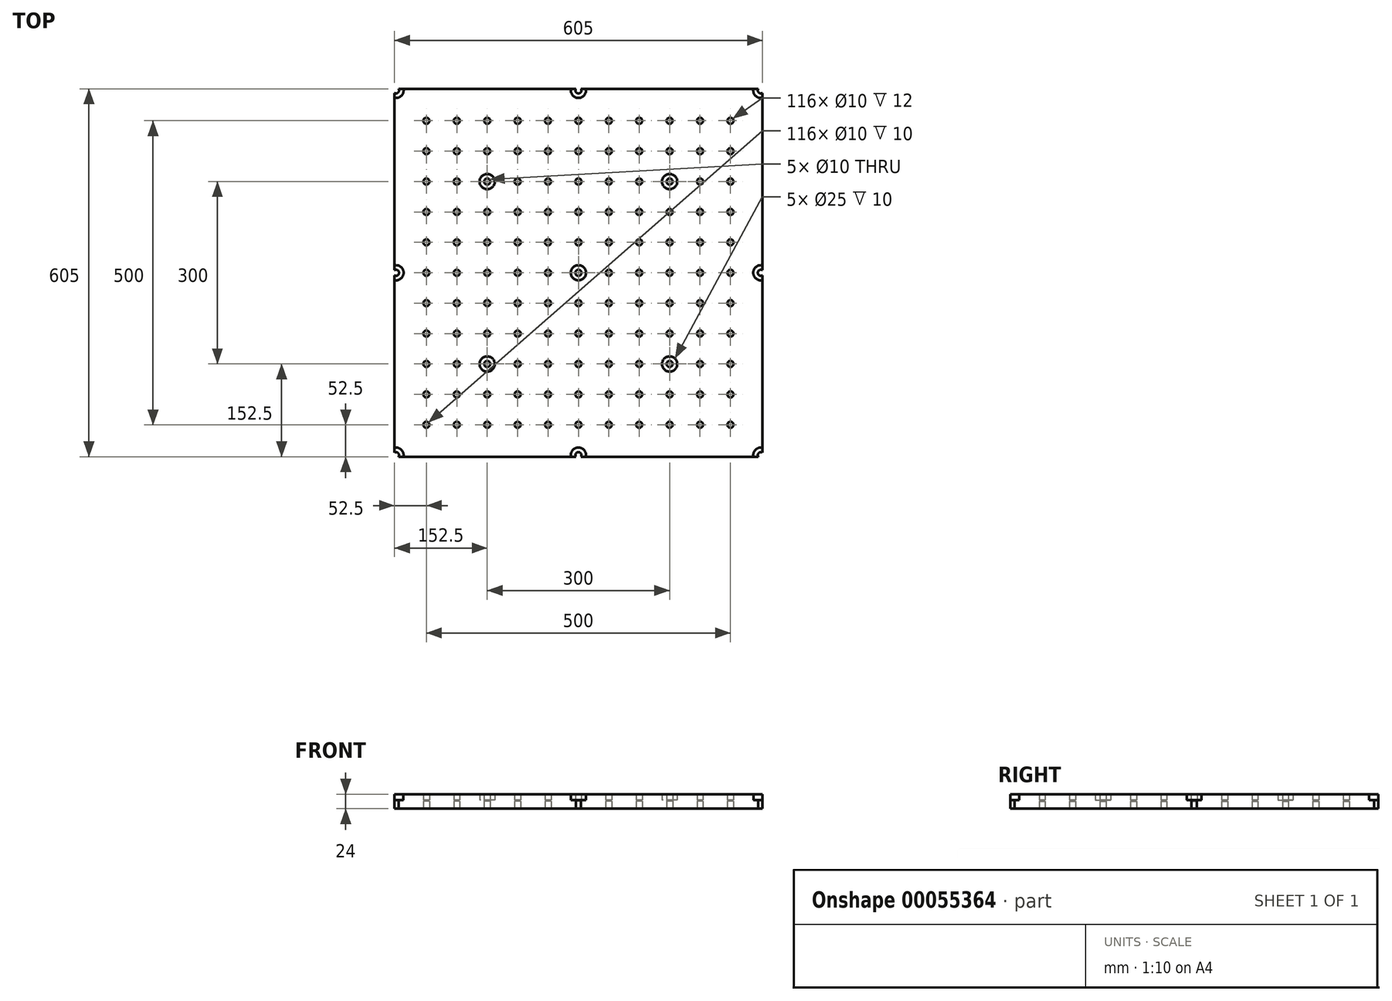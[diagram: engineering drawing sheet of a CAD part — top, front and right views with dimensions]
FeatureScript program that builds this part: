
annotation { "Feature Type Name" : "Feature", "Feature Type Description" : "" }
export const myFeature = defineFeature(function(context is Context, id is Id, definition is map)
    precondition{}
    {
        {
            var Q0;
            Q0=qCreatedBy(makeId("Top.planeOp"),FACE);
            var sketch = newSketch(context, id + "F0", { "sketchPlane" : qUnion([Q0])});
            skLineSegment(sketch, "E0.rect.bottom", {"start": v(295.67, 302.5) * mm, "end": v(4.33, 302.5) * mm});
            skLineSegment(sketch, "E0.rect.top", {"start": v(295.67, -302.5) * mm, "end": v(4.33, -302.5) * mm});
            skLineSegment(sketch, "E0.rect.left", {"start": v(302.5, 295.67) * mm, "end": v(302.5, 4.33) * mm});
            skLineSegment(sketch, "E0.rect.right", {"start": v(-302.5, 295.67) * mm, "end": v(-302.5, 4.33) * mm});
            skPoint(sketch, "E0.rect.middle", {"position": v(0, 0) * mm});
            skArc(sketch, "E1", {"start": v(-295.67, -302.5) * mm, "mid": v(-296.46, -296.46) * mm, "end": v(-302.5, -295.67) * mm});
            skCircle(sketch, "E2.0.1.0", {"center": v(-300, -250) * mm, "radius": 5 * mm, "construction": true});
            skCircle(sketch, "E2.0.2.0", {"center": v(-300, -200) * mm, "radius": 5 * mm, "construction": true});
            skCircle(sketch, "E2.0.3.0", {"center": v(-300, -150) * mm, "radius": 5 * mm, "construction": true});
            skCircle(sketch, "E2.0.4.0", {"center": v(-300, -100) * mm, "radius": 5 * mm, "construction": true});
            skCircle(sketch, "E2.0.5.0", {"center": v(-300, -50) * mm, "radius": 5 * mm, "construction": true});
            skArc(sketch, "E2.0.6.0", {"start": v(-302.5, -4.33) * mm, "mid": v(-295, 0) * mm, "end": v(-302.5, 4.33) * mm});
            skCircle(sketch, "E2.0.7.0", {"center": v(-300, 50) * mm, "radius": 5 * mm, "construction": true});
            skCircle(sketch, "E2.0.8.0", {"center": v(-300, 100) * mm, "radius": 5 * mm, "construction": true});
            skCircle(sketch, "E2.0.9.0", {"center": v(-300, 150) * mm, "radius": 5 * mm, "construction": true});
            skCircle(sketch, "E2.0.10.0", {"center": v(-300, 200) * mm, "radius": 5 * mm, "construction": true});
            skCircle(sketch, "E2.0.11.0", {"center": v(-300, 250) * mm, "radius": 5 * mm, "construction": true});
            skArc(sketch, "E2.0.12.0", {"start": v(-302.5, 295.67) * mm, "mid": v(-296.46, 296.46) * mm, "end": v(-295.67, 302.5) * mm});
            skCircle(sketch, "E2.1.0.0", {"center": v(-250, -300) * mm, "radius": 5 * mm, "construction": true});
            skCircle(sketch, "E2.1.1.0", {"center": v(-250, -250) * mm, "radius": 5 * mm});
            skCircle(sketch, "E2.1.2.0", {"center": v(-250, -200) * mm, "radius": 5 * mm});
            skCircle(sketch, "E2.1.3.0", {"center": v(-250, -150) * mm, "radius": 5 * mm});
            skCircle(sketch, "E2.1.4.0", {"center": v(-250, -100) * mm, "radius": 5 * mm});
            skCircle(sketch, "E2.1.5.0", {"center": v(-250, -50) * mm, "radius": 5 * mm});
            skCircle(sketch, "E2.1.6.0", {"center": v(-250, 0) * mm, "radius": 5 * mm});
            skCircle(sketch, "E2.1.7.0", {"center": v(-250, 50) * mm, "radius": 5 * mm});
            skCircle(sketch, "E2.1.8.0", {"center": v(-250, 100) * mm, "radius": 5 * mm});
            skCircle(sketch, "E2.1.9.0", {"center": v(-250, 150) * mm, "radius": 5 * mm});
            skCircle(sketch, "E2.1.10.0", {"center": v(-250, 200) * mm, "radius": 5 * mm});
            skCircle(sketch, "E2.1.11.0", {"center": v(-250, 250) * mm, "radius": 5 * mm});
            skCircle(sketch, "E2.1.12.0", {"center": v(-250, 300) * mm, "radius": 5 * mm, "construction": true});
            skCircle(sketch, "E2.2.0.0", {"center": v(-200, -300) * mm, "radius": 5 * mm, "construction": true});
            skCircle(sketch, "E2.2.1.0", {"center": v(-200, -250) * mm, "radius": 5 * mm});
            skCircle(sketch, "E2.2.2.0", {"center": v(-200, -200) * mm, "radius": 5 * mm});
            skCircle(sketch, "E2.2.3.0", {"center": v(-200, -150) * mm, "radius": 5 * mm});
            skCircle(sketch, "E2.2.4.0", {"center": v(-200, -100) * mm, "radius": 5 * mm});
            skCircle(sketch, "E2.2.5.0", {"center": v(-200, -50) * mm, "radius": 5 * mm});
            skCircle(sketch, "E2.2.6.0", {"center": v(-200, 0) * mm, "radius": 5 * mm});
            skCircle(sketch, "E2.2.7.0", {"center": v(-200, 50) * mm, "radius": 5 * mm});
            skCircle(sketch, "E2.2.8.0", {"center": v(-200, 100) * mm, "radius": 5 * mm});
            skCircle(sketch, "E2.2.9.0", {"center": v(-200, 150) * mm, "radius": 5 * mm});
            skCircle(sketch, "E2.2.10.0", {"center": v(-200, 200) * mm, "radius": 5 * mm});
            skCircle(sketch, "E2.2.11.0", {"center": v(-200, 250) * mm, "radius": 5 * mm});
            skCircle(sketch, "E2.2.12.0", {"center": v(-200, 300) * mm, "radius": 5 * mm, "construction": true});
            skCircle(sketch, "E2.3.0.0", {"center": v(-150, -300) * mm, "radius": 5 * mm, "construction": true});
            skCircle(sketch, "E2.3.1.0", {"center": v(-150, -250) * mm, "radius": 5 * mm});
            skCircle(sketch, "E2.3.2.0", {"center": v(-150, -200) * mm, "radius": 5 * mm});
            skCircle(sketch, "E2.3.3.0", {"center": v(-150, -150) * mm, "radius": 5 * mm});
            skCircle(sketch, "E2.3.4.0", {"center": v(-150, -100) * mm, "radius": 5 * mm});
            skCircle(sketch, "E2.3.5.0", {"center": v(-150, -50) * mm, "radius": 5 * mm});
            skCircle(sketch, "E2.3.6.0", {"center": v(-150, 0) * mm, "radius": 5 * mm});
            skCircle(sketch, "E2.3.7.0", {"center": v(-150, 50) * mm, "radius": 5 * mm});
            skCircle(sketch, "E2.3.8.0", {"center": v(-150, 100) * mm, "radius": 5 * mm});
            skCircle(sketch, "E2.3.9.0", {"center": v(-150, 150) * mm, "radius": 5 * mm});
            skCircle(sketch, "E2.3.10.0", {"center": v(-150, 200) * mm, "radius": 5 * mm});
            skCircle(sketch, "E2.3.11.0", {"center": v(-150, 250) * mm, "radius": 5 * mm});
            skCircle(sketch, "E2.3.12.0", {"center": v(-150, 300) * mm, "radius": 5 * mm, "construction": true});
            skCircle(sketch, "E2.4.0.0", {"center": v(-100, -300) * mm, "radius": 5 * mm, "construction": true});
            skCircle(sketch, "E2.4.1.0", {"center": v(-100, -250) * mm, "radius": 5 * mm});
            skCircle(sketch, "E2.4.2.0", {"center": v(-100, -200) * mm, "radius": 5 * mm});
            skCircle(sketch, "E2.4.3.0", {"center": v(-100, -150) * mm, "radius": 5 * mm});
            skCircle(sketch, "E2.4.4.0", {"center": v(-100, -100) * mm, "radius": 5 * mm});
            skCircle(sketch, "E2.4.5.0", {"center": v(-100, -50) * mm, "radius": 5 * mm});
            skCircle(sketch, "E2.4.6.0", {"center": v(-100, 0) * mm, "radius": 5 * mm});
            skCircle(sketch, "E2.4.7.0", {"center": v(-100, 50) * mm, "radius": 5 * mm});
            skCircle(sketch, "E2.4.8.0", {"center": v(-100, 100) * mm, "radius": 5 * mm});
            skCircle(sketch, "E2.4.9.0", {"center": v(-100, 150) * mm, "radius": 5 * mm});
            skCircle(sketch, "E2.4.10.0", {"center": v(-100, 200) * mm, "radius": 5 * mm});
            skCircle(sketch, "E2.4.11.0", {"center": v(-100, 250) * mm, "radius": 5 * mm});
            skCircle(sketch, "E2.4.12.0", {"center": v(-100, 300) * mm, "radius": 5 * mm, "construction": true});
            skCircle(sketch, "E2.5.0.0", {"center": v(-50, -300) * mm, "radius": 5 * mm, "construction": true});
            skCircle(sketch, "E2.5.1.0", {"center": v(-50, -250) * mm, "radius": 5 * mm});
            skCircle(sketch, "E2.5.2.0", {"center": v(-50, -200) * mm, "radius": 5 * mm});
            skCircle(sketch, "E2.5.3.0", {"center": v(-50, -150) * mm, "radius": 5 * mm});
            skCircle(sketch, "E2.5.4.0", {"center": v(-50, -100) * mm, "radius": 5 * mm});
            skCircle(sketch, "E2.5.5.0", {"center": v(-50, -50) * mm, "radius": 5 * mm});
            skCircle(sketch, "E2.5.6.0", {"center": v(-50, 0) * mm, "radius": 5 * mm});
            skCircle(sketch, "E2.5.7.0", {"center": v(-50, 50) * mm, "radius": 5 * mm});
            skCircle(sketch, "E2.5.8.0", {"center": v(-50, 100) * mm, "radius": 5 * mm});
            skCircle(sketch, "E2.5.9.0", {"center": v(-50, 150) * mm, "radius": 5 * mm});
            skCircle(sketch, "E2.5.10.0", {"center": v(-50, 200) * mm, "radius": 5 * mm});
            skCircle(sketch, "E2.5.11.0", {"center": v(-50, 250) * mm, "radius": 5 * mm});
            skCircle(sketch, "E2.5.12.0", {"center": v(-50, 300) * mm, "radius": 5 * mm, "construction": true});
            skArc(sketch, "E2.6.0.0", {"start": v(4.33, -302.5) * mm, "mid": v(0, -295) * mm, "end": v(-4.33, -302.5) * mm});
            skCircle(sketch, "E2.6.1.0", {"center": v(0, -250) * mm, "radius": 5 * mm});
            skCircle(sketch, "E2.6.2.0", {"center": v(0, -200) * mm, "radius": 5 * mm});
            skCircle(sketch, "E2.6.3.0", {"center": v(0, -150) * mm, "radius": 5 * mm});
            skCircle(sketch, "E2.6.4.0", {"center": v(0, -100) * mm, "radius": 5 * mm});
            skCircle(sketch, "E2.6.5.0", {"center": v(0, -50) * mm, "radius": 5 * mm});
            skCircle(sketch, "E2.6.6.0", {"center": v(0, 0) * mm, "radius": 5 * mm});
            skCircle(sketch, "E2.6.7.0", {"center": v(0, 50) * mm, "radius": 5 * mm});
            skCircle(sketch, "E2.6.8.0", {"center": v(0, 100) * mm, "radius": 5 * mm});
            skCircle(sketch, "E2.6.9.0", {"center": v(0, 150) * mm, "radius": 5 * mm});
            skCircle(sketch, "E2.6.10.0", {"center": v(0, 200) * mm, "radius": 5 * mm});
            skCircle(sketch, "E2.6.11.0", {"center": v(0, 250) * mm, "radius": 5 * mm});
            skArc(sketch, "E2.6.12.0", {"start": v(-4.33, 302.5) * mm, "mid": v(0, 295) * mm, "end": v(4.33, 302.5) * mm});
            skCircle(sketch, "E2.7.0.0", {"center": v(50, -300) * mm, "radius": 5 * mm, "construction": true});
            skCircle(sketch, "E2.7.1.0", {"center": v(50, -250) * mm, "radius": 5 * mm});
            skCircle(sketch, "E2.7.2.0", {"center": v(50, -200) * mm, "radius": 5 * mm});
            skCircle(sketch, "E2.7.3.0", {"center": v(50, -150) * mm, "radius": 5 * mm});
            skCircle(sketch, "E2.7.4.0", {"center": v(50, -100) * mm, "radius": 5 * mm});
            skCircle(sketch, "E2.7.5.0", {"center": v(50, -50) * mm, "radius": 5 * mm});
            skCircle(sketch, "E2.7.6.0", {"center": v(50, 0) * mm, "radius": 5 * mm});
            skCircle(sketch, "E2.7.7.0", {"center": v(50, 50) * mm, "radius": 5 * mm});
            skCircle(sketch, "E2.7.8.0", {"center": v(50, 100) * mm, "radius": 5 * mm});
            skCircle(sketch, "E2.7.9.0", {"center": v(50, 150) * mm, "radius": 5 * mm});
            skCircle(sketch, "E2.7.10.0", {"center": v(50, 200) * mm, "radius": 5 * mm});
            skCircle(sketch, "E2.7.11.0", {"center": v(50, 250) * mm, "radius": 5 * mm});
            skCircle(sketch, "E2.7.12.0", {"center": v(50, 300) * mm, "radius": 5 * mm, "construction": true});
            skCircle(sketch, "E2.8.0.0", {"center": v(100, -300) * mm, "radius": 5 * mm, "construction": true});
            skCircle(sketch, "E2.8.1.0", {"center": v(100, -250) * mm, "radius": 5 * mm});
            skCircle(sketch, "E2.8.2.0", {"center": v(100, -200) * mm, "radius": 5 * mm});
            skCircle(sketch, "E2.8.3.0", {"center": v(100, -150) * mm, "radius": 5 * mm});
            skCircle(sketch, "E2.8.4.0", {"center": v(100, -100) * mm, "radius": 5 * mm});
            skCircle(sketch, "E2.8.5.0", {"center": v(100, -50) * mm, "radius": 5 * mm});
            skCircle(sketch, "E2.8.6.0", {"center": v(100, 0) * mm, "radius": 5 * mm});
            skCircle(sketch, "E2.8.7.0", {"center": v(100, 50) * mm, "radius": 5 * mm});
            skCircle(sketch, "E2.8.8.0", {"center": v(100, 100) * mm, "radius": 5 * mm});
            skCircle(sketch, "E2.8.9.0", {"center": v(100, 150) * mm, "radius": 5 * mm});
            skCircle(sketch, "E2.8.10.0", {"center": v(100, 200) * mm, "radius": 5 * mm});
            skCircle(sketch, "E2.8.11.0", {"center": v(100, 250) * mm, "radius": 5 * mm});
            skCircle(sketch, "E2.8.12.0", {"center": v(100, 300) * mm, "radius": 5 * mm, "construction": true});
            skCircle(sketch, "E2.9.0.0", {"center": v(150, -300) * mm, "radius": 5 * mm, "construction": true});
            skCircle(sketch, "E2.9.1.0", {"center": v(150, -250) * mm, "radius": 5 * mm});
            skCircle(sketch, "E2.9.2.0", {"center": v(150, -200) * mm, "radius": 5 * mm});
            skCircle(sketch, "E2.9.3.0", {"center": v(150, -150) * mm, "radius": 5 * mm});
            skCircle(sketch, "E2.9.4.0", {"center": v(150, -100) * mm, "radius": 5 * mm});
            skCircle(sketch, "E2.9.5.0", {"center": v(150, -50) * mm, "radius": 5 * mm});
            skCircle(sketch, "E2.9.6.0", {"center": v(150, 0) * mm, "radius": 5 * mm});
            skCircle(sketch, "E2.9.7.0", {"center": v(150, 50) * mm, "radius": 5 * mm});
            skCircle(sketch, "E2.9.8.0", {"center": v(150, 100) * mm, "radius": 5 * mm});
            skCircle(sketch, "E2.9.9.0", {"center": v(150, 150) * mm, "radius": 5 * mm});
            skCircle(sketch, "E2.9.10.0", {"center": v(150, 200) * mm, "radius": 5 * mm});
            skCircle(sketch, "E2.9.11.0", {"center": v(150, 250) * mm, "radius": 5 * mm});
            skCircle(sketch, "E2.9.12.0", {"center": v(150, 300) * mm, "radius": 5 * mm, "construction": true});
            skCircle(sketch, "E2.10.0.0", {"center": v(200, -300) * mm, "radius": 5 * mm, "construction": true});
            skCircle(sketch, "E2.10.1.0", {"center": v(200, -250) * mm, "radius": 5 * mm});
            skCircle(sketch, "E2.10.2.0", {"center": v(200, -200) * mm, "radius": 5 * mm});
            skCircle(sketch, "E2.10.3.0", {"center": v(200, -150) * mm, "radius": 5 * mm});
            skCircle(sketch, "E2.10.4.0", {"center": v(200, -100) * mm, "radius": 5 * mm});
            skCircle(sketch, "E2.10.5.0", {"center": v(200, -50) * mm, "radius": 5 * mm});
            skCircle(sketch, "E2.10.6.0", {"center": v(200, 0) * mm, "radius": 5 * mm});
            skCircle(sketch, "E2.10.7.0", {"center": v(200, 50) * mm, "radius": 5 * mm});
            skCircle(sketch, "E2.10.8.0", {"center": v(200, 100) * mm, "radius": 5 * mm});
            skCircle(sketch, "E2.10.9.0", {"center": v(200, 150) * mm, "radius": 5 * mm});
            skCircle(sketch, "E2.10.10.0", {"center": v(200, 200) * mm, "radius": 5 * mm});
            skCircle(sketch, "E2.10.11.0", {"center": v(200, 250) * mm, "radius": 5 * mm});
            skCircle(sketch, "E2.10.12.0", {"center": v(200, 300) * mm, "radius": 5 * mm, "construction": true});
            skCircle(sketch, "E2.11.0.0", {"center": v(250, -300) * mm, "radius": 5 * mm, "construction": true});
            skCircle(sketch, "E2.11.1.0", {"center": v(250, -250) * mm, "radius": 5 * mm});
            skCircle(sketch, "E2.11.2.0", {"center": v(250, -200) * mm, "radius": 5 * mm});
            skCircle(sketch, "E2.11.3.0", {"center": v(250, -150) * mm, "radius": 5 * mm});
            skCircle(sketch, "E2.11.4.0", {"center": v(250, -100) * mm, "radius": 5 * mm});
            skCircle(sketch, "E2.11.5.0", {"center": v(250, -50) * mm, "radius": 5 * mm});
            skCircle(sketch, "E2.11.6.0", {"center": v(250, 0) * mm, "radius": 5 * mm});
            skCircle(sketch, "E2.11.7.0", {"center": v(250, 50) * mm, "radius": 5 * mm});
            skCircle(sketch, "E2.11.8.0", {"center": v(250, 100) * mm, "radius": 5 * mm});
            skCircle(sketch, "E2.11.9.0", {"center": v(250, 150) * mm, "radius": 5 * mm});
            skCircle(sketch, "E2.11.10.0", {"center": v(250, 200) * mm, "radius": 5 * mm});
            skCircle(sketch, "E2.11.11.0", {"center": v(250, 250) * mm, "radius": 5 * mm});
            skCircle(sketch, "E2.11.12.0", {"center": v(250, 300) * mm, "radius": 5 * mm, "construction": true});
            skArc(sketch, "E2.12.0.0", {"start": v(302.5, -295.67) * mm, "mid": v(296.46, -296.46) * mm, "end": v(295.67, -302.5) * mm});
            skCircle(sketch, "E2.12.1.0", {"center": v(300, -250) * mm, "radius": 5 * mm, "construction": true});
            skCircle(sketch, "E2.12.2.0", {"center": v(300, -200) * mm, "radius": 5 * mm, "construction": true});
            skCircle(sketch, "E2.12.3.0", {"center": v(300, -150) * mm, "radius": 5 * mm, "construction": true});
            skCircle(sketch, "E2.12.4.0", {"center": v(300, -100) * mm, "radius": 5 * mm, "construction": true});
            skCircle(sketch, "E2.12.5.0", {"center": v(300, -50) * mm, "radius": 5 * mm, "construction": true});
            skArc(sketch, "E2.12.6.0", {"start": v(302.5, 4.33) * mm, "mid": v(295, 0) * mm, "end": v(302.5, -4.33) * mm});
            skCircle(sketch, "E2.12.7.0", {"center": v(300, 50) * mm, "radius": 5 * mm, "construction": true});
            skCircle(sketch, "E2.12.8.0", {"center": v(300, 100) * mm, "radius": 5 * mm, "construction": true});
            skCircle(sketch, "E2.12.9.0", {"center": v(300, 150) * mm, "radius": 5 * mm, "construction": true});
            skCircle(sketch, "E2.12.10.0", {"center": v(300, 200) * mm, "radius": 5 * mm, "construction": true});
            skCircle(sketch, "E2.12.11.0", {"center": v(300, 250) * mm, "radius": 5 * mm, "construction": true});
            skArc(sketch, "E2.12.12.0", {"start": v(295.67, 302.5) * mm, "mid": v(296.46, 296.46) * mm, "end": v(302.5, 295.67) * mm});
            skLineSegment(sketch, "E2.direction1", {"start": v(-300, -300) * mm, "end": v(-250, -300) * mm, "construction": true});
            skLineSegment(sketch, "E2.direction2", {"start": v(-300, -300) * mm, "end": v(-300, -250) * mm, "construction": true});
            skLineSegment(sketch, "E3.trimOffspring", {"start": v(-4.33, -302.5) * mm, "end": v(-295.67, -302.5) * mm});
            skLineSegment(sketch, "E4.trimOffspring", {"start": v(-302.5, -4.33) * mm, "end": v(-302.5, -295.67) * mm});
            skPoint(sketch, "E5.orphan", {"position": v(-302.5, -302.5) * mm});
            skPoint(sketch, "E6.orphan", {"position": v(-302.5, 302.5) * mm});
            skLineSegment(sketch, "E7.trimOffspring", {"start": v(-4.33, 302.5) * mm, "end": v(-295.67, 302.5) * mm});
            skPoint(sketch, "E8.orphan", {"position": v(302.5, 302.5) * mm});
            skLineSegment(sketch, "E9.trimOffspring", {"start": v(302.5, -4.33) * mm, "end": v(302.5, -295.67) * mm});
            skPoint(sketch, "E10.orphan", {"position": v(302.5, -302.5) * mm});
            skSolve(sketch);
        }
        {
            var Q0;
            Q0 = qSketchRegion(id + "F0", true);
            extrude(context, id + "F1", {"entities" : qUnion([Q0]), "depth" : 12 * mm});
        }
        {
            var Q0;
            Q0=makeQuery(id+"F1.opExtrude","CAP_FACE",FACE,{"disambiguationData":[OSD([sQuery(id+"F0.wireOp",EDGE,"E0.rect.bottom"),sQuery(id+"F0.wireOp",EDGE,"E0.rect.top"),sQuery(id+"F0.wireOp",EDGE,"E0.rect.left"),sQuery(id+"F0.wireOp",EDGE,"E0.rect.right"),sQuery(id+"F0.wireOp",EDGE,"E1"),sQuery(id+"F0.wireOp",EDGE,"E2.0.6.0"),sQuery(id+"F0.wireOp",EDGE,"E2.0.12.0"),sQuery(id+"F0.wireOp",EDGE,"E2.3.3.0"),sQuery(id+"F0.wireOp",EDGE,"E2.3.9.0"),sQuery(id+"F0.wireOp",EDGE,"E2.6.0.0"),sQuery(id+"F0.wireOp",EDGE,"E2.6.6.0"),sQuery(id+"F0.wireOp",EDGE,"E2.6.12.0"),sQuery(id+"F0.wireOp",EDGE,"E2.9.3.0"),sQuery(id+"F0.wireOp",EDGE,"E2.9.9.0"),sQuery(id+"F0.wireOp",EDGE,"E2.12.0.0"),sQuery(id+"F0.wireOp",EDGE,"E2.12.6.0"),sQuery(id+"F0.wireOp",EDGE,"E2.12.12.0"),sQuery(id+"F0.wireOp",EDGE,"E3.trimOffspring"),sQuery(id+"F0.wireOp",EDGE,"E4.trimOffspring"),sQuery(id+"F0.wireOp",EDGE,"E7.trimOffspring"),sQuery(id+"F0.wireOp",EDGE,"E9.trimOffspring")])],"isStart":false});
            var sketch = newSketch(context, id + "F2", { "sketchPlane" : qUnion([Q0])});
            skLineSegment(sketch, "E11.rect.bottom", {"start": v(295.67, 302.5) * mm, "end": v(4.33, 302.5) * mm, "construction": true});
            skLineSegment(sketch, "E11.rect.top", {"start": v(295.67, -302.5) * mm, "end": v(4.33, -302.5) * mm, "construction": true});
            skLineSegment(sketch, "E11.rect.left", {"start": v(302.5, 295.67) * mm, "end": v(302.5, 4.33) * mm, "construction": true});
            skLineSegment(sketch, "E11.rect.right", {"start": v(-302.5, 295.67) * mm, "end": v(-302.5, 4.33) * mm, "construction": true});
            skPoint(sketch, "E11.rect.middle", {"position": v(0, 0) * mm});
            skArc(sketch, "E12", {"start": v(-295.67, -302.5) * mm, "mid": v(-296.46, -296.46) * mm, "end": v(-302.5, -295.67) * mm, "construction": true});
            skCircle(sketch, "E13.0.1.0", {"center": v(-300, -250) * mm, "radius": 5 * mm, "construction": true});
            skCircle(sketch, "E13.0.2.0", {"center": v(-300, -200) * mm, "radius": 5 * mm, "construction": true});
            skCircle(sketch, "E13.0.3.0", {"center": v(-300, -150) * mm, "radius": 5 * mm, "construction": true});
            skCircle(sketch, "E13.0.4.0", {"center": v(-300, -100) * mm, "radius": 5 * mm, "construction": true});
            skCircle(sketch, "E13.0.5.0", {"center": v(-300, -50) * mm, "radius": 5 * mm, "construction": true});
            skArc(sketch, "E13.0.6.0", {"start": v(-302.5, -4.33) * mm, "mid": v(-295, 0) * mm, "end": v(-302.5, 4.33) * mm, "construction": true});
            skCircle(sketch, "E13.0.7.0", {"center": v(-300, 50) * mm, "radius": 5 * mm, "construction": true});
            skCircle(sketch, "E13.0.8.0", {"center": v(-300, 100) * mm, "radius": 5 * mm, "construction": true});
            skCircle(sketch, "E13.0.9.0", {"center": v(-300, 150) * mm, "radius": 5 * mm, "construction": true});
            skCircle(sketch, "E13.0.10.0", {"center": v(-300, 200) * mm, "radius": 5 * mm, "construction": true});
            skCircle(sketch, "E13.0.11.0", {"center": v(-300, 250) * mm, "radius": 5 * mm, "construction": true});
            skArc(sketch, "E13.0.12.0", {"start": v(-302.5, 295.67) * mm, "mid": v(-296.46, 296.46) * mm, "end": v(-295.67, 302.5) * mm, "construction": true});
            skCircle(sketch, "E13.1.0.0", {"center": v(-250, -300) * mm, "radius": 5 * mm, "construction": true});
            skCircle(sketch, "E13.1.1.0", {"center": v(-250, -250) * mm, "radius": 5 * mm, "construction": true});
            skCircle(sketch, "E13.1.2.0", {"center": v(-250, -200) * mm, "radius": 5 * mm, "construction": true});
            skCircle(sketch, "E13.1.3.0", {"center": v(-250, -150) * mm, "radius": 5 * mm, "construction": true});
            skCircle(sketch, "E13.1.4.0", {"center": v(-250, -100) * mm, "radius": 5 * mm, "construction": true});
            skCircle(sketch, "E13.1.5.0", {"center": v(-250, -50) * mm, "radius": 5 * mm, "construction": true});
            skCircle(sketch, "E13.1.6.0", {"center": v(-250, 0) * mm, "radius": 5 * mm, "construction": true});
            skCircle(sketch, "E13.1.7.0", {"center": v(-250, 50) * mm, "radius": 5 * mm, "construction": true});
            skCircle(sketch, "E13.1.8.0", {"center": v(-250, 100) * mm, "radius": 5 * mm, "construction": true});
            skCircle(sketch, "E13.1.9.0", {"center": v(-250, 150) * mm, "radius": 5 * mm, "construction": true});
            skCircle(sketch, "E13.1.10.0", {"center": v(-250, 200) * mm, "radius": 5 * mm, "construction": true});
            skCircle(sketch, "E13.1.11.0", {"center": v(-250, 250) * mm, "radius": 5 * mm, "construction": true});
            skCircle(sketch, "E13.1.12.0", {"center": v(-250, 300) * mm, "radius": 5 * mm, "construction": true});
            skCircle(sketch, "E13.2.0.0", {"center": v(-200, -300) * mm, "radius": 5 * mm, "construction": true});
            skCircle(sketch, "E13.2.1.0", {"center": v(-200, -250) * mm, "radius": 5 * mm, "construction": true});
            skCircle(sketch, "E13.2.2.0", {"center": v(-200, -200) * mm, "radius": 5 * mm, "construction": true});
            skCircle(sketch, "E13.2.3.0", {"center": v(-200, -150) * mm, "radius": 5 * mm, "construction": true});
            skCircle(sketch, "E13.2.4.0", {"center": v(-200, -100) * mm, "radius": 5 * mm, "construction": true});
            skCircle(sketch, "E13.2.5.0", {"center": v(-200, -50) * mm, "radius": 5 * mm, "construction": true});
            skCircle(sketch, "E13.2.6.0", {"center": v(-200, 0) * mm, "radius": 5 * mm, "construction": true});
            skCircle(sketch, "E13.2.7.0", {"center": v(-200, 50) * mm, "radius": 5 * mm, "construction": true});
            skCircle(sketch, "E13.2.8.0", {"center": v(-200, 100) * mm, "radius": 5 * mm, "construction": true});
            skCircle(sketch, "E13.2.9.0", {"center": v(-200, 150) * mm, "radius": 5 * mm, "construction": true});
            skCircle(sketch, "E13.2.10.0", {"center": v(-200, 200) * mm, "radius": 5 * mm, "construction": true});
            skCircle(sketch, "E13.2.11.0", {"center": v(-200, 250) * mm, "radius": 5 * mm, "construction": true});
            skCircle(sketch, "E13.2.12.0", {"center": v(-200, 300) * mm, "radius": 5 * mm, "construction": true});
            skCircle(sketch, "E13.3.0.0", {"center": v(-150, -300) * mm, "radius": 5 * mm, "construction": true});
            skCircle(sketch, "E13.3.1.0", {"center": v(-150, -250) * mm, "radius": 5 * mm, "construction": true});
            skCircle(sketch, "E13.3.2.0", {"center": v(-150, -200) * mm, "radius": 5 * mm, "construction": true});
            skCircle(sketch, "E13.3.3.0", {"center": v(-150, -150) * mm, "radius": 5 * mm, "construction": true});
            skCircle(sketch, "E13.3.4.0", {"center": v(-150, -100) * mm, "radius": 5 * mm, "construction": true});
            skCircle(sketch, "E13.3.5.0", {"center": v(-150, -50) * mm, "radius": 5 * mm, "construction": true});
            skCircle(sketch, "E13.3.6.0", {"center": v(-150, 0) * mm, "radius": 5 * mm, "construction": true});
            skCircle(sketch, "E13.3.7.0", {"center": v(-150, 50) * mm, "radius": 5 * mm, "construction": true});
            skCircle(sketch, "E13.3.8.0", {"center": v(-150, 100) * mm, "radius": 5 * mm, "construction": true});
            skCircle(sketch, "E13.3.9.0", {"center": v(-150, 150) * mm, "radius": 5 * mm, "construction": true});
            skCircle(sketch, "E13.3.10.0", {"center": v(-150, 200) * mm, "radius": 5 * mm, "construction": true});
            skCircle(sketch, "E13.3.11.0", {"center": v(-150, 250) * mm, "radius": 5 * mm, "construction": true});
            skCircle(sketch, "E13.3.12.0", {"center": v(-150, 300) * mm, "radius": 5 * mm, "construction": true});
            skCircle(sketch, "E13.4.0.0", {"center": v(-100, -300) * mm, "radius": 5 * mm, "construction": true});
            skCircle(sketch, "E13.4.1.0", {"center": v(-100, -250) * mm, "radius": 5 * mm, "construction": true});
            skCircle(sketch, "E13.4.2.0", {"center": v(-100, -200) * mm, "radius": 5 * mm, "construction": true});
            skCircle(sketch, "E13.4.3.0", {"center": v(-100, -150) * mm, "radius": 5 * mm, "construction": true});
            skCircle(sketch, "E13.4.4.0", {"center": v(-100, -100) * mm, "radius": 5 * mm, "construction": true});
            skCircle(sketch, "E13.4.5.0", {"center": v(-100, -50) * mm, "radius": 5 * mm, "construction": true});
            skCircle(sketch, "E13.4.6.0", {"center": v(-100, 0) * mm, "radius": 5 * mm, "construction": true});
            skCircle(sketch, "E13.4.7.0", {"center": v(-100, 50) * mm, "radius": 5 * mm, "construction": true});
            skCircle(sketch, "E13.4.8.0", {"center": v(-100, 100) * mm, "radius": 5 * mm, "construction": true});
            skCircle(sketch, "E13.4.9.0", {"center": v(-100, 150) * mm, "radius": 5 * mm, "construction": true});
            skCircle(sketch, "E13.4.10.0", {"center": v(-100, 200) * mm, "radius": 5 * mm, "construction": true});
            skCircle(sketch, "E13.4.11.0", {"center": v(-100, 250) * mm, "radius": 5 * mm, "construction": true});
            skCircle(sketch, "E13.4.12.0", {"center": v(-100, 300) * mm, "radius": 5 * mm, "construction": true});
            skCircle(sketch, "E13.5.0.0", {"center": v(-50, -300) * mm, "radius": 5 * mm, "construction": true});
            skCircle(sketch, "E13.5.1.0", {"center": v(-50, -250) * mm, "radius": 5 * mm, "construction": true});
            skCircle(sketch, "E13.5.2.0", {"center": v(-50, -200) * mm, "radius": 5 * mm, "construction": true});
            skCircle(sketch, "E13.5.3.0", {"center": v(-50, -150) * mm, "radius": 5 * mm, "construction": true});
            skCircle(sketch, "E13.5.4.0", {"center": v(-50, -100) * mm, "radius": 5 * mm, "construction": true});
            skCircle(sketch, "E13.5.5.0", {"center": v(-50, -50) * mm, "radius": 5 * mm, "construction": true});
            skCircle(sketch, "E13.5.6.0", {"center": v(-50, 0) * mm, "radius": 5 * mm, "construction": true});
            skCircle(sketch, "E13.5.7.0", {"center": v(-50, 50) * mm, "radius": 5 * mm, "construction": true});
            skCircle(sketch, "E13.5.8.0", {"center": v(-50, 100) * mm, "radius": 5 * mm, "construction": true});
            skCircle(sketch, "E13.5.9.0", {"center": v(-50, 150) * mm, "radius": 5 * mm, "construction": true});
            skCircle(sketch, "E13.5.10.0", {"center": v(-50, 200) * mm, "radius": 5 * mm, "construction": true});
            skCircle(sketch, "E13.5.11.0", {"center": v(-50, 250) * mm, "radius": 5 * mm, "construction": true});
            skCircle(sketch, "E13.5.12.0", {"center": v(-50, 300) * mm, "radius": 5 * mm, "construction": true});
            skArc(sketch, "E13.6.0.0", {"start": v(4.33, -302.5) * mm, "mid": v(0, -295) * mm, "end": v(-4.33, -302.5) * mm, "construction": true});
            skCircle(sketch, "E13.6.1.0", {"center": v(0, -250) * mm, "radius": 5 * mm, "construction": true});
            skCircle(sketch, "E13.6.2.0", {"center": v(0, -200) * mm, "radius": 5 * mm, "construction": true});
            skCircle(sketch, "E13.6.3.0", {"center": v(0, -150) * mm, "radius": 5 * mm, "construction": true});
            skCircle(sketch, "E13.6.4.0", {"center": v(0, -100) * mm, "radius": 5 * mm, "construction": true});
            skCircle(sketch, "E13.6.5.0", {"center": v(0, -50) * mm, "radius": 5 * mm, "construction": true});
            skCircle(sketch, "E13.6.6.0", {"center": v(0, 0) * mm, "radius": 5 * mm, "construction": true});
            skCircle(sketch, "E13.6.7.0", {"center": v(0, 50) * mm, "radius": 5 * mm, "construction": true});
            skCircle(sketch, "E13.6.8.0", {"center": v(0, 100) * mm, "radius": 5 * mm, "construction": true});
            skCircle(sketch, "E13.6.9.0", {"center": v(0, 150) * mm, "radius": 5 * mm, "construction": true});
            skCircle(sketch, "E13.6.10.0", {"center": v(0, 200) * mm, "radius": 5 * mm, "construction": true});
            skCircle(sketch, "E13.6.11.0", {"center": v(0, 250) * mm, "radius": 5 * mm, "construction": true});
            skArc(sketch, "E13.6.12.0", {"start": v(-4.33, 302.5) * mm, "mid": v(0, 295) * mm, "end": v(4.33, 302.5) * mm, "construction": true});
            skCircle(sketch, "E13.7.0.0", {"center": v(50, -300) * mm, "radius": 5 * mm, "construction": true});
            skCircle(sketch, "E13.7.1.0", {"center": v(50, -250) * mm, "radius": 5 * mm, "construction": true});
            skCircle(sketch, "E13.7.2.0", {"center": v(50, -200) * mm, "radius": 5 * mm, "construction": true});
            skCircle(sketch, "E13.7.3.0", {"center": v(50, -150) * mm, "radius": 5 * mm, "construction": true});
            skCircle(sketch, "E13.7.4.0", {"center": v(50, -100) * mm, "radius": 5 * mm, "construction": true});
            skCircle(sketch, "E13.7.5.0", {"center": v(50, -50) * mm, "radius": 5 * mm, "construction": true});
            skCircle(sketch, "E13.7.6.0", {"center": v(50, 0) * mm, "radius": 5 * mm, "construction": true});
            skCircle(sketch, "E13.7.7.0", {"center": v(50, 50) * mm, "radius": 5 * mm, "construction": true});
            skCircle(sketch, "E13.7.8.0", {"center": v(50, 100) * mm, "radius": 5 * mm, "construction": true});
            skCircle(sketch, "E13.7.9.0", {"center": v(50, 150) * mm, "radius": 5 * mm, "construction": true});
            skCircle(sketch, "E13.7.10.0", {"center": v(50, 200) * mm, "radius": 5 * mm, "construction": true});
            skCircle(sketch, "E13.7.11.0", {"center": v(50, 250) * mm, "radius": 5 * mm, "construction": true});
            skCircle(sketch, "E13.7.12.0", {"center": v(50, 300) * mm, "radius": 5 * mm, "construction": true});
            skCircle(sketch, "E13.8.0.0", {"center": v(100, -300) * mm, "radius": 5 * mm, "construction": true});
            skCircle(sketch, "E13.8.1.0", {"center": v(100, -250) * mm, "radius": 5 * mm, "construction": true});
            skCircle(sketch, "E13.8.2.0", {"center": v(100, -200) * mm, "radius": 5 * mm, "construction": true});
            skCircle(sketch, "E13.8.3.0", {"center": v(100, -150) * mm, "radius": 5 * mm, "construction": true});
            skCircle(sketch, "E13.8.4.0", {"center": v(100, -100) * mm, "radius": 5 * mm, "construction": true});
            skCircle(sketch, "E13.8.5.0", {"center": v(100, -50) * mm, "radius": 5 * mm, "construction": true});
            skCircle(sketch, "E13.8.6.0", {"center": v(100, 0) * mm, "radius": 5 * mm, "construction": true});
            skCircle(sketch, "E13.8.7.0", {"center": v(100, 50) * mm, "radius": 5 * mm, "construction": true});
            skCircle(sketch, "E13.8.8.0", {"center": v(100, 100) * mm, "radius": 5 * mm, "construction": true});
            skCircle(sketch, "E13.8.9.0", {"center": v(100, 150) * mm, "radius": 5 * mm, "construction": true});
            skCircle(sketch, "E13.8.10.0", {"center": v(100, 200) * mm, "radius": 5 * mm, "construction": true});
            skCircle(sketch, "E13.8.11.0", {"center": v(100, 250) * mm, "radius": 5 * mm, "construction": true});
            skCircle(sketch, "E13.8.12.0", {"center": v(100, 300) * mm, "radius": 5 * mm, "construction": true});
            skCircle(sketch, "E13.9.0.0", {"center": v(150, -300) * mm, "radius": 5 * mm, "construction": true});
            skCircle(sketch, "E13.9.1.0", {"center": v(150, -250) * mm, "radius": 5 * mm, "construction": true});
            skCircle(sketch, "E13.9.2.0", {"center": v(150, -200) * mm, "radius": 5 * mm, "construction": true});
            skCircle(sketch, "E13.9.3.0", {"center": v(150, -150) * mm, "radius": 5 * mm, "construction": true});
            skCircle(sketch, "E13.9.4.0", {"center": v(150, -100) * mm, "radius": 5 * mm, "construction": true});
            skCircle(sketch, "E13.9.5.0", {"center": v(150, -50) * mm, "radius": 5 * mm, "construction": true});
            skCircle(sketch, "E13.9.6.0", {"center": v(150, 0) * mm, "radius": 5 * mm, "construction": true});
            skCircle(sketch, "E13.9.7.0", {"center": v(150, 50) * mm, "radius": 5 * mm, "construction": true});
            skCircle(sketch, "E13.9.8.0", {"center": v(150, 100) * mm, "radius": 5 * mm, "construction": true});
            skCircle(sketch, "E13.9.9.0", {"center": v(150, 150) * mm, "radius": 5 * mm, "construction": true});
            skCircle(sketch, "E13.9.10.0", {"center": v(150, 200) * mm, "radius": 5 * mm, "construction": true});
            skCircle(sketch, "E13.9.11.0", {"center": v(150, 250) * mm, "radius": 5 * mm, "construction": true});
            skCircle(sketch, "E13.9.12.0", {"center": v(150, 300) * mm, "radius": 5 * mm, "construction": true});
            skCircle(sketch, "E13.10.0.0", {"center": v(200, -300) * mm, "radius": 5 * mm, "construction": true});
            skCircle(sketch, "E13.10.1.0", {"center": v(200, -250) * mm, "radius": 5 * mm, "construction": true});
            skCircle(sketch, "E13.10.2.0", {"center": v(200, -200) * mm, "radius": 5 * mm, "construction": true});
            skCircle(sketch, "E13.10.3.0", {"center": v(200, -150) * mm, "radius": 5 * mm, "construction": true});
            skCircle(sketch, "E13.10.4.0", {"center": v(200, -100) * mm, "radius": 5 * mm, "construction": true});
            skCircle(sketch, "E13.10.5.0", {"center": v(200, -50) * mm, "radius": 5 * mm, "construction": true});
            skCircle(sketch, "E13.10.6.0", {"center": v(200, 0) * mm, "radius": 5 * mm, "construction": true});
            skCircle(sketch, "E13.10.7.0", {"center": v(200, 50) * mm, "radius": 5 * mm, "construction": true});
            skCircle(sketch, "E13.10.8.0", {"center": v(200, 100) * mm, "radius": 5 * mm, "construction": true});
            skCircle(sketch, "E13.10.9.0", {"center": v(200, 150) * mm, "radius": 5 * mm, "construction": true});
            skCircle(sketch, "E13.10.10.0", {"center": v(200, 200) * mm, "radius": 5 * mm, "construction": true});
            skCircle(sketch, "E13.10.11.0", {"center": v(200, 250) * mm, "radius": 5 * mm, "construction": true});
            skCircle(sketch, "E13.10.12.0", {"center": v(200, 300) * mm, "radius": 5 * mm, "construction": true});
            skCircle(sketch, "E13.11.0.0", {"center": v(250, -300) * mm, "radius": 5 * mm, "construction": true});
            skCircle(sketch, "E13.11.1.0", {"center": v(250, -250) * mm, "radius": 5 * mm, "construction": true});
            skCircle(sketch, "E13.11.2.0", {"center": v(250, -200) * mm, "radius": 5 * mm, "construction": true});
            skCircle(sketch, "E13.11.3.0", {"center": v(250, -150) * mm, "radius": 5 * mm, "construction": true});
            skCircle(sketch, "E13.11.4.0", {"center": v(250, -100) * mm, "radius": 5 * mm, "construction": true});
            skCircle(sketch, "E13.11.5.0", {"center": v(250, -50) * mm, "radius": 5 * mm, "construction": true});
            skCircle(sketch, "E13.11.6.0", {"center": v(250, 0) * mm, "radius": 5 * mm, "construction": true});
            skCircle(sketch, "E13.11.7.0", {"center": v(250, 50) * mm, "radius": 5 * mm, "construction": true});
            skCircle(sketch, "E13.11.8.0", {"center": v(250, 100) * mm, "radius": 5 * mm, "construction": true});
            skCircle(sketch, "E13.11.9.0", {"center": v(250, 150) * mm, "radius": 5 * mm, "construction": true});
            skCircle(sketch, "E13.11.10.0", {"center": v(250, 200) * mm, "radius": 5 * mm, "construction": true});
            skCircle(sketch, "E13.11.11.0", {"center": v(250, 250) * mm, "radius": 5 * mm, "construction": true});
            skCircle(sketch, "E13.11.12.0", {"center": v(250, 300) * mm, "radius": 5 * mm, "construction": true});
            skArc(sketch, "E13.12.0.0", {"start": v(302.5, -295.67) * mm, "mid": v(296.46, -296.46) * mm, "end": v(295.67, -302.5) * mm, "construction": true});
            skCircle(sketch, "E13.12.1.0", {"center": v(300, -250) * mm, "radius": 5 * mm, "construction": true});
            skCircle(sketch, "E13.12.2.0", {"center": v(300, -200) * mm, "radius": 5 * mm, "construction": true});
            skCircle(sketch, "E13.12.3.0", {"center": v(300, -150) * mm, "radius": 5 * mm, "construction": true});
            skCircle(sketch, "E13.12.4.0", {"center": v(300, -100) * mm, "radius": 5 * mm, "construction": true});
            skCircle(sketch, "E13.12.5.0", {"center": v(300, -50) * mm, "radius": 5 * mm, "construction": true});
            skArc(sketch, "E13.12.6.0", {"start": v(302.5, 4.33) * mm, "mid": v(295, 0) * mm, "end": v(302.5, -4.33) * mm, "construction": true});
            skCircle(sketch, "E13.12.7.0", {"center": v(300, 50) * mm, "radius": 5 * mm, "construction": true});
            skCircle(sketch, "E13.12.8.0", {"center": v(300, 100) * mm, "radius": 5 * mm, "construction": true});
            skCircle(sketch, "E13.12.9.0", {"center": v(300, 150) * mm, "radius": 5 * mm, "construction": true});
            skCircle(sketch, "E13.12.10.0", {"center": v(300, 200) * mm, "radius": 5 * mm, "construction": true});
            skCircle(sketch, "E13.12.11.0", {"center": v(300, 250) * mm, "radius": 5 * mm, "construction": true});
            skArc(sketch, "E13.12.12.0", {"start": v(295.67, 302.5) * mm, "mid": v(296.46, 296.46) * mm, "end": v(302.5, 295.67) * mm, "construction": true});
            skLineSegment(sketch, "E13.direction1", {"start": v(-300, -300) * mm, "end": v(-250, -300) * mm, "construction": true});
            skLineSegment(sketch, "E13.direction2", {"start": v(-300, -300) * mm, "end": v(-300, -250) * mm, "construction": true});
            skLineSegment(sketch, "E14.trimOffspring", {"start": v(-4.33, -302.5) * mm, "end": v(-295.67, -302.5) * mm, "construction": true});
            skLineSegment(sketch, "E15.trimOffspring", {"start": v(-302.5, -4.33) * mm, "end": v(-302.5, -295.67) * mm, "construction": true});
            skPoint(sketch, "E16.orphan", {"position": v(-302.5, -302.5) * mm});
            skPoint(sketch, "E17.orphan", {"position": v(-302.5, 302.5) * mm});
            skLineSegment(sketch, "E18.trimOffspring", {"start": v(-4.33, 302.5) * mm, "end": v(-295.67, 302.5) * mm, "construction": true});
            skPoint(sketch, "E19.orphan", {"position": v(302.5, 302.5) * mm});
            skLineSegment(sketch, "E20.trimOffspring", {"start": v(302.5, -4.33) * mm, "end": v(302.5, -295.67) * mm, "construction": true});
            skPoint(sketch, "E21.orphan", {"position": v(302.5, -302.5) * mm});
            skCircle(sketch, "E22", {"center": v(0, 0) * mm, "radius": 12.5 * mm});
            skCircle(sketch, "E23", {"center": v(-150, 150) * mm, "radius": 12.5 * mm});
            skCircle(sketch, "E24", {"center": v(-150, -150) * mm, "radius": 12.5 * mm});
            skCircle(sketch, "E25", {"center": v(150, -150) * mm, "radius": 12.5 * mm});
            skCircle(sketch, "E26", {"center": v(150, 150) * mm, "radius": 12.5 * mm});
            skArc(sketch, "E27", {"start": v(-302.5, 287.75) * mm, "mid": v(-291.16, 291.16) * mm, "end": v(-287.75, 302.5) * mm});
            skArc(sketch, "E28", {"start": v(-287.75, -302.5) * mm, "mid": v(-291.16, -291.16) * mm, "end": v(-302.5, -287.75) * mm});
            skArc(sketch, "E29", {"start": v(302.5, -287.75) * mm, "mid": v(291.16, -291.16) * mm, "end": v(287.75, -302.5) * mm});
            skArc(sketch, "E30", {"start": v(287.75, 302.5) * mm, "mid": v(291.16, 291.16) * mm, "end": v(302.5, 287.75) * mm});
            skArc(sketch, "E31", {"start": v(-12.25, 302.5) * mm, "mid": v(0, 287.5) * mm, "end": v(12.25, 302.5) * mm});
            skArc(sketch, "E32", {"start": v(-302.5, -12.25) * mm, "mid": v(-287.5, 0) * mm, "end": v(-302.5, 12.25) * mm});
            skArc(sketch, "E33", {"start": v(12.25, -302.5) * mm, "mid": v(0, -287.5) * mm, "end": v(-12.25, -302.5) * mm});
            skArc(sketch, "E34", {"start": v(302.5, 12.25) * mm, "mid": v(287.5, 0) * mm, "end": v(302.5, -12.25) * mm});
            skLineSegment(sketch, "E35", {"start": v(302.5, 287.75) * mm, "end": v(302.5, 12.25) * mm});
            skLineSegment(sketch, "E36", {"start": v(302.5, -12.25) * mm, "end": v(302.5, -287.75) * mm});
            skLineSegment(sketch, "E37", {"start": v(287.75, -302.5) * mm, "end": v(12.25, -302.5) * mm});
            skLineSegment(sketch, "E38", {"start": v(-12.25, -302.5) * mm, "end": v(-287.75, -302.5) * mm});
            skLineSegment(sketch, "E39", {"start": v(-302.5, -287.75) * mm, "end": v(-302.5, -12.25) * mm});
            skLineSegment(sketch, "E40", {"start": v(-302.5, 12.25) * mm, "end": v(-302.5, 287.75) * mm});
            skLineSegment(sketch, "E41", {"start": v(-287.75, 302.5) * mm, "end": v(-12.25, 302.5) * mm});
            skLineSegment(sketch, "E42", {"start": v(12.25, 302.5) * mm, "end": v(287.75, 302.5) * mm});
            skSolve(sketch);
        }
        {
            var Q0;
            Q0=makeQuery(id+"F2.imprint","IMPRINT",FACE,{"disambiguationData":[TD([[makeQuery(id+"F2.imprint","IMPRINT",EDGE,{"derivedFrom":sQuery(id+"F2.wireOp",EDGE,"E22")}),-1.0]])]});
            extrude(context, id + "F3", {"entities" : qUnion([Q0]), "depth" : 12 * mm});
        }
        {
            var Q0;
            Q0=makeQuery(id+"F1.opExtrude","CAP_FACE",FACE,{"disambiguationData":[OSD([sQuery(id+"F0.wireOp",EDGE,"E0.rect.bottom"),sQuery(id+"F0.wireOp",EDGE,"E0.rect.top"),sQuery(id+"F0.wireOp",EDGE,"E0.rect.left"),sQuery(id+"F0.wireOp",EDGE,"E0.rect.right"),sQuery(id+"F0.wireOp",EDGE,"E1"),sQuery(id+"F0.wireOp",EDGE,"E2.0.6.0"),sQuery(id+"F0.wireOp",EDGE,"E2.0.12.0"),sQuery(id+"F0.wireOp",EDGE,"E2.3.3.0"),sQuery(id+"F0.wireOp",EDGE,"E2.3.9.0"),sQuery(id+"F0.wireOp",EDGE,"E2.6.0.0"),sQuery(id+"F0.wireOp",EDGE,"E2.6.6.0"),sQuery(id+"F0.wireOp",EDGE,"E2.6.12.0"),sQuery(id+"F0.wireOp",EDGE,"E2.9.3.0"),sQuery(id+"F0.wireOp",EDGE,"E2.9.9.0"),sQuery(id+"F0.wireOp",EDGE,"E2.12.0.0"),sQuery(id+"F0.wireOp",EDGE,"E2.12.6.0"),sQuery(id+"F0.wireOp",EDGE,"E2.12.12.0"),sQuery(id+"F0.wireOp",EDGE,"E3.trimOffspring"),sQuery(id+"F0.wireOp",EDGE,"E4.trimOffspring"),sQuery(id+"F0.wireOp",EDGE,"E7.trimOffspring"),sQuery(id+"F0.wireOp",EDGE,"E9.trimOffspring")])],"isStart":false});
            var sketch = newSketch(context, id + "F4", { "sketchPlane" : qUnion([Q0])});
            skLineSegment(sketch, "E43.rect.bottom", {"start": v(295.67, 302.5) * mm, "end": v(4.33, 302.5) * mm});
            skLineSegment(sketch, "E43.rect.top", {"start": v(295.67, -302.5) * mm, "end": v(4.33, -302.5) * mm});
            skLineSegment(sketch, "E43.rect.left", {"start": v(302.5, 295.67) * mm, "end": v(302.5, 4.33) * mm});
            skLineSegment(sketch, "E43.rect.right", {"start": v(-302.5, 295.67) * mm, "end": v(-302.5, 4.33) * mm});
            skPoint(sketch, "E43.rect.middle", {"position": v(0, 0) * mm});
            skArc(sketch, "E44", {"start": v(-295.67, -302.5) * mm, "mid": v(-296.46, -296.46) * mm, "end": v(-302.5, -295.67) * mm});
            skCircle(sketch, "E45.0.1.0", {"center": v(-300, -250) * mm, "radius": 5 * mm, "construction": true});
            skCircle(sketch, "E45.0.2.0", {"center": v(-300, -200) * mm, "radius": 5 * mm, "construction": true});
            skCircle(sketch, "E45.0.3.0", {"center": v(-300, -150) * mm, "radius": 5 * mm, "construction": true});
            skCircle(sketch, "E45.0.4.0", {"center": v(-300, -100) * mm, "radius": 5 * mm, "construction": true});
            skCircle(sketch, "E45.0.5.0", {"center": v(-300, -50) * mm, "radius": 5 * mm, "construction": true});
            skArc(sketch, "E45.0.6.0", {"start": v(-302.5, -4.33) * mm, "mid": v(-295, 0) * mm, "end": v(-302.5, 4.33) * mm});
            skCircle(sketch, "E45.0.7.0", {"center": v(-300, 50) * mm, "radius": 5 * mm, "construction": true});
            skCircle(sketch, "E45.0.8.0", {"center": v(-300, 100) * mm, "radius": 5 * mm, "construction": true});
            skCircle(sketch, "E45.0.9.0", {"center": v(-300, 150) * mm, "radius": 5 * mm, "construction": true});
            skCircle(sketch, "E45.0.10.0", {"center": v(-300, 200) * mm, "radius": 5 * mm, "construction": true});
            skCircle(sketch, "E45.0.11.0", {"center": v(-300, 250) * mm, "radius": 5 * mm, "construction": true});
            skArc(sketch, "E45.0.12.0", {"start": v(-302.5, 295.67) * mm, "mid": v(-296.46, 296.46) * mm, "end": v(-295.67, 302.5) * mm});
            skCircle(sketch, "E45.1.0.0", {"center": v(-250, -300) * mm, "radius": 5 * mm, "construction": true});
            skCircle(sketch, "E45.1.1.0", {"center": v(-250, -250) * mm, "radius": 5 * mm, "construction": true});
            skCircle(sketch, "E45.1.2.0", {"center": v(-250, -200) * mm, "radius": 5 * mm, "construction": true});
            skCircle(sketch, "E45.1.3.0", {"center": v(-250, -150) * mm, "radius": 5 * mm, "construction": true});
            skCircle(sketch, "E45.1.4.0", {"center": v(-250, -100) * mm, "radius": 5 * mm, "construction": true});
            skCircle(sketch, "E45.1.5.0", {"center": v(-250, -50) * mm, "radius": 5 * mm, "construction": true});
            skCircle(sketch, "E45.1.6.0", {"center": v(-250, 0) * mm, "radius": 5 * mm, "construction": true});
            skCircle(sketch, "E45.1.7.0", {"center": v(-250, 50) * mm, "radius": 5 * mm, "construction": true});
            skCircle(sketch, "E45.1.8.0", {"center": v(-250, 100) * mm, "radius": 5 * mm, "construction": true});
            skCircle(sketch, "E45.1.9.0", {"center": v(-250, 150) * mm, "radius": 5 * mm, "construction": true});
            skCircle(sketch, "E45.1.10.0", {"center": v(-250, 200) * mm, "radius": 5 * mm, "construction": true});
            skCircle(sketch, "E45.1.11.0", {"center": v(-250, 250) * mm, "radius": 5 * mm, "construction": true});
            skCircle(sketch, "E45.1.12.0", {"center": v(-250, 300) * mm, "radius": 5 * mm, "construction": true});
            skCircle(sketch, "E45.2.0.0", {"center": v(-200, -300) * mm, "radius": 5 * mm, "construction": true});
            skCircle(sketch, "E45.2.1.0", {"center": v(-200, -250) * mm, "radius": 5 * mm, "construction": true});
            skCircle(sketch, "E45.2.2.0", {"center": v(-200, -200) * mm, "radius": 5 * mm, "construction": true});
            skCircle(sketch, "E45.2.3.0", {"center": v(-200, -150) * mm, "radius": 5 * mm, "construction": true});
            skCircle(sketch, "E45.2.4.0", {"center": v(-200, -100) * mm, "radius": 5 * mm, "construction": true});
            skCircle(sketch, "E45.2.5.0", {"center": v(-200, -50) * mm, "radius": 5 * mm, "construction": true});
            skCircle(sketch, "E45.2.6.0", {"center": v(-200, 0) * mm, "radius": 5 * mm, "construction": true});
            skCircle(sketch, "E45.2.7.0", {"center": v(-200, 50) * mm, "radius": 5 * mm, "construction": true});
            skCircle(sketch, "E45.2.8.0", {"center": v(-200, 100) * mm, "radius": 5 * mm, "construction": true});
            skCircle(sketch, "E45.2.9.0", {"center": v(-200, 150) * mm, "radius": 5 * mm, "construction": true});
            skCircle(sketch, "E45.2.10.0", {"center": v(-200, 200) * mm, "radius": 5 * mm, "construction": true});
            skCircle(sketch, "E45.2.11.0", {"center": v(-200, 250) * mm, "radius": 5 * mm, "construction": true});
            skCircle(sketch, "E45.2.12.0", {"center": v(-200, 300) * mm, "radius": 5 * mm, "construction": true});
            skCircle(sketch, "E45.3.0.0", {"center": v(-150, -300) * mm, "radius": 5 * mm, "construction": true});
            skCircle(sketch, "E45.3.1.0", {"center": v(-150, -250) * mm, "radius": 5 * mm, "construction": true});
            skCircle(sketch, "E45.3.2.0", {"center": v(-150, -200) * mm, "radius": 5 * mm, "construction": true});
            skCircle(sketch, "E45.3.3.0", {"center": v(-150, -150) * mm, "radius": 5 * mm});
            skCircle(sketch, "E45.3.4.0", {"center": v(-150, -100) * mm, "radius": 5 * mm, "construction": true});
            skCircle(sketch, "E45.3.5.0", {"center": v(-150, -50) * mm, "radius": 5 * mm, "construction": true});
            skCircle(sketch, "E45.3.6.0", {"center": v(-150, 0) * mm, "radius": 5 * mm, "construction": true});
            skCircle(sketch, "E45.3.7.0", {"center": v(-150, 50) * mm, "radius": 5 * mm, "construction": true});
            skCircle(sketch, "E45.3.8.0", {"center": v(-150, 100) * mm, "radius": 5 * mm, "construction": true});
            skCircle(sketch, "E45.3.9.0", {"center": v(-150, 150) * mm, "radius": 5 * mm});
            skCircle(sketch, "E45.3.10.0", {"center": v(-150, 200) * mm, "radius": 5 * mm, "construction": true});
            skCircle(sketch, "E45.3.11.0", {"center": v(-150, 250) * mm, "radius": 5 * mm, "construction": true});
            skCircle(sketch, "E45.3.12.0", {"center": v(-150, 300) * mm, "radius": 5 * mm, "construction": true});
            skCircle(sketch, "E45.4.0.0", {"center": v(-100, -300) * mm, "radius": 5 * mm, "construction": true});
            skCircle(sketch, "E45.4.1.0", {"center": v(-100, -250) * mm, "radius": 5 * mm, "construction": true});
            skCircle(sketch, "E45.4.2.0", {"center": v(-100, -200) * mm, "radius": 5 * mm, "construction": true});
            skCircle(sketch, "E45.4.3.0", {"center": v(-100, -150) * mm, "radius": 5 * mm, "construction": true});
            skCircle(sketch, "E45.4.4.0", {"center": v(-100, -100) * mm, "radius": 5 * mm, "construction": true});
            skCircle(sketch, "E45.4.5.0", {"center": v(-100, -50) * mm, "radius": 5 * mm, "construction": true});
            skCircle(sketch, "E45.4.6.0", {"center": v(-100, 0) * mm, "radius": 5 * mm, "construction": true});
            skCircle(sketch, "E45.4.7.0", {"center": v(-100, 50) * mm, "radius": 5 * mm, "construction": true});
            skCircle(sketch, "E45.4.8.0", {"center": v(-100, 100) * mm, "radius": 5 * mm, "construction": true});
            skCircle(sketch, "E45.4.9.0", {"center": v(-100, 150) * mm, "radius": 5 * mm, "construction": true});
            skCircle(sketch, "E45.4.10.0", {"center": v(-100, 200) * mm, "radius": 5 * mm, "construction": true});
            skCircle(sketch, "E45.4.11.0", {"center": v(-100, 250) * mm, "radius": 5 * mm, "construction": true});
            skCircle(sketch, "E45.4.12.0", {"center": v(-100, 300) * mm, "radius": 5 * mm, "construction": true});
            skCircle(sketch, "E45.5.0.0", {"center": v(-50, -300) * mm, "radius": 5 * mm, "construction": true});
            skCircle(sketch, "E45.5.1.0", {"center": v(-50, -250) * mm, "radius": 5 * mm, "construction": true});
            skCircle(sketch, "E45.5.2.0", {"center": v(-50, -200) * mm, "radius": 5 * mm, "construction": true});
            skCircle(sketch, "E45.5.3.0", {"center": v(-50, -150) * mm, "radius": 5 * mm, "construction": true});
            skCircle(sketch, "E45.5.4.0", {"center": v(-50, -100) * mm, "radius": 5 * mm, "construction": true});
            skCircle(sketch, "E45.5.5.0", {"center": v(-50, -50) * mm, "radius": 5 * mm, "construction": true});
            skCircle(sketch, "E45.5.6.0", {"center": v(-50, 0) * mm, "radius": 5 * mm, "construction": true});
            skCircle(sketch, "E45.5.7.0", {"center": v(-50, 50) * mm, "radius": 5 * mm, "construction": true});
            skCircle(sketch, "E45.5.8.0", {"center": v(-50, 100) * mm, "radius": 5 * mm, "construction": true});
            skCircle(sketch, "E45.5.9.0", {"center": v(-50, 150) * mm, "radius": 5 * mm, "construction": true});
            skCircle(sketch, "E45.5.10.0", {"center": v(-50, 200) * mm, "radius": 5 * mm, "construction": true});
            skCircle(sketch, "E45.5.11.0", {"center": v(-50, 250) * mm, "radius": 5 * mm, "construction": true});
            skCircle(sketch, "E45.5.12.0", {"center": v(-50, 300) * mm, "radius": 5 * mm, "construction": true});
            skArc(sketch, "E45.6.0.0", {"start": v(4.33, -302.5) * mm, "mid": v(0, -295) * mm, "end": v(-4.33, -302.5) * mm});
            skCircle(sketch, "E45.6.1.0", {"center": v(0, -250) * mm, "radius": 5 * mm, "construction": true});
            skCircle(sketch, "E45.6.2.0", {"center": v(0, -200) * mm, "radius": 5 * mm, "construction": true});
            skCircle(sketch, "E45.6.3.0", {"center": v(0, -150) * mm, "radius": 5 * mm, "construction": true});
            skCircle(sketch, "E45.6.4.0", {"center": v(0, -100) * mm, "radius": 5 * mm, "construction": true});
            skCircle(sketch, "E45.6.5.0", {"center": v(0, -50) * mm, "radius": 5 * mm, "construction": true});
            skCircle(sketch, "E45.6.6.0", {"center": v(0, 0) * mm, "radius": 5 * mm});
            skCircle(sketch, "E45.6.7.0", {"center": v(0, 50) * mm, "radius": 5 * mm, "construction": true});
            skCircle(sketch, "E45.6.8.0", {"center": v(0, 100) * mm, "radius": 5 * mm, "construction": true});
            skCircle(sketch, "E45.6.9.0", {"center": v(0, 150) * mm, "radius": 5 * mm, "construction": true});
            skCircle(sketch, "E45.6.10.0", {"center": v(0, 200) * mm, "radius": 5 * mm, "construction": true});
            skCircle(sketch, "E45.6.11.0", {"center": v(0, 250) * mm, "radius": 5 * mm, "construction": true});
            skArc(sketch, "E45.6.12.0", {"start": v(-4.33, 302.5) * mm, "mid": v(0, 295) * mm, "end": v(4.33, 302.5) * mm});
            skCircle(sketch, "E45.7.0.0", {"center": v(50, -300) * mm, "radius": 5 * mm, "construction": true});
            skCircle(sketch, "E45.7.1.0", {"center": v(50, -250) * mm, "radius": 5 * mm, "construction": true});
            skCircle(sketch, "E45.7.2.0", {"center": v(50, -200) * mm, "radius": 5 * mm, "construction": true});
            skCircle(sketch, "E45.7.3.0", {"center": v(50, -150) * mm, "radius": 5 * mm, "construction": true});
            skCircle(sketch, "E45.7.4.0", {"center": v(50, -100) * mm, "radius": 5 * mm, "construction": true});
            skCircle(sketch, "E45.7.5.0", {"center": v(50, -50) * mm, "radius": 5 * mm, "construction": true});
            skCircle(sketch, "E45.7.6.0", {"center": v(50, 0) * mm, "radius": 5 * mm, "construction": true});
            skCircle(sketch, "E45.7.7.0", {"center": v(50, 50) * mm, "radius": 5 * mm, "construction": true});
            skCircle(sketch, "E45.7.8.0", {"center": v(50, 100) * mm, "radius": 5 * mm, "construction": true});
            skCircle(sketch, "E45.7.9.0", {"center": v(50, 150) * mm, "radius": 5 * mm, "construction": true});
            skCircle(sketch, "E45.7.10.0", {"center": v(50, 200) * mm, "radius": 5 * mm, "construction": true});
            skCircle(sketch, "E45.7.11.0", {"center": v(50, 250) * mm, "radius": 5 * mm, "construction": true});
            skCircle(sketch, "E45.7.12.0", {"center": v(50, 300) * mm, "radius": 5 * mm, "construction": true});
            skCircle(sketch, "E45.8.0.0", {"center": v(100, -300) * mm, "radius": 5 * mm, "construction": true});
            skCircle(sketch, "E45.8.1.0", {"center": v(100, -250) * mm, "radius": 5 * mm, "construction": true});
            skCircle(sketch, "E45.8.2.0", {"center": v(100, -200) * mm, "radius": 5 * mm, "construction": true});
            skCircle(sketch, "E45.8.3.0", {"center": v(100, -150) * mm, "radius": 5 * mm, "construction": true});
            skCircle(sketch, "E45.8.4.0", {"center": v(100, -100) * mm, "radius": 5 * mm, "construction": true});
            skCircle(sketch, "E45.8.5.0", {"center": v(100, -50) * mm, "radius": 5 * mm, "construction": true});
            skCircle(sketch, "E45.8.6.0", {"center": v(100, 0) * mm, "radius": 5 * mm, "construction": true});
            skCircle(sketch, "E45.8.7.0", {"center": v(100, 50) * mm, "radius": 5 * mm, "construction": true});
            skCircle(sketch, "E45.8.8.0", {"center": v(100, 100) * mm, "radius": 5 * mm, "construction": true});
            skCircle(sketch, "E45.8.9.0", {"center": v(100, 150) * mm, "radius": 5 * mm, "construction": true});
            skCircle(sketch, "E45.8.10.0", {"center": v(100, 200) * mm, "radius": 5 * mm, "construction": true});
            skCircle(sketch, "E45.8.11.0", {"center": v(100, 250) * mm, "radius": 5 * mm, "construction": true});
            skCircle(sketch, "E45.8.12.0", {"center": v(100, 300) * mm, "radius": 5 * mm, "construction": true});
            skCircle(sketch, "E45.9.0.0", {"center": v(150, -300) * mm, "radius": 5 * mm, "construction": true});
            skCircle(sketch, "E45.9.1.0", {"center": v(150, -250) * mm, "radius": 5 * mm, "construction": true});
            skCircle(sketch, "E45.9.2.0", {"center": v(150, -200) * mm, "radius": 5 * mm, "construction": true});
            skCircle(sketch, "E45.9.3.0", {"center": v(150, -150) * mm, "radius": 5 * mm});
            skCircle(sketch, "E45.9.4.0", {"center": v(150, -100) * mm, "radius": 5 * mm, "construction": true});
            skCircle(sketch, "E45.9.5.0", {"center": v(150, -50) * mm, "radius": 5 * mm, "construction": true});
            skCircle(sketch, "E45.9.6.0", {"center": v(150, 0) * mm, "radius": 5 * mm, "construction": true});
            skCircle(sketch, "E45.9.7.0", {"center": v(150, 50) * mm, "radius": 5 * mm, "construction": true});
            skCircle(sketch, "E45.9.8.0", {"center": v(150, 100) * mm, "radius": 5 * mm, "construction": true});
            skCircle(sketch, "E45.9.9.0", {"center": v(150, 150) * mm, "radius": 5 * mm});
            skCircle(sketch, "E45.9.10.0", {"center": v(150, 200) * mm, "radius": 5 * mm, "construction": true});
            skCircle(sketch, "E45.9.11.0", {"center": v(150, 250) * mm, "radius": 5 * mm, "construction": true});
            skCircle(sketch, "E45.9.12.0", {"center": v(150, 300) * mm, "radius": 5 * mm, "construction": true});
            skCircle(sketch, "E45.10.0.0", {"center": v(200, -300) * mm, "radius": 5 * mm, "construction": true});
            skCircle(sketch, "E45.10.1.0", {"center": v(200, -250) * mm, "radius": 5 * mm, "construction": true});
            skCircle(sketch, "E45.10.2.0", {"center": v(200, -200) * mm, "radius": 5 * mm, "construction": true});
            skCircle(sketch, "E45.10.3.0", {"center": v(200, -150) * mm, "radius": 5 * mm, "construction": true});
            skCircle(sketch, "E45.10.4.0", {"center": v(200, -100) * mm, "radius": 5 * mm, "construction": true});
            skCircle(sketch, "E45.10.5.0", {"center": v(200, -50) * mm, "radius": 5 * mm, "construction": true});
            skCircle(sketch, "E45.10.6.0", {"center": v(200, 0) * mm, "radius": 5 * mm, "construction": true});
            skCircle(sketch, "E45.10.7.0", {"center": v(200, 50) * mm, "radius": 5 * mm, "construction": true});
            skCircle(sketch, "E45.10.8.0", {"center": v(200, 100) * mm, "radius": 5 * mm, "construction": true});
            skCircle(sketch, "E45.10.9.0", {"center": v(200, 150) * mm, "radius": 5 * mm, "construction": true});
            skCircle(sketch, "E45.10.10.0", {"center": v(200, 200) * mm, "radius": 5 * mm, "construction": true});
            skCircle(sketch, "E45.10.11.0", {"center": v(200, 250) * mm, "radius": 5 * mm, "construction": true});
            skCircle(sketch, "E45.10.12.0", {"center": v(200, 300) * mm, "radius": 5 * mm, "construction": true});
            skCircle(sketch, "E45.11.0.0", {"center": v(250, -300) * mm, "radius": 5 * mm, "construction": true});
            skCircle(sketch, "E45.11.1.0", {"center": v(250, -250) * mm, "radius": 5 * mm, "construction": true});
            skCircle(sketch, "E45.11.2.0", {"center": v(250, -200) * mm, "radius": 5 * mm, "construction": true});
            skCircle(sketch, "E45.11.3.0", {"center": v(250, -150) * mm, "radius": 5 * mm, "construction": true});
            skCircle(sketch, "E45.11.4.0", {"center": v(250, -100) * mm, "radius": 5 * mm, "construction": true});
            skCircle(sketch, "E45.11.5.0", {"center": v(250, -50) * mm, "radius": 5 * mm, "construction": true});
            skCircle(sketch, "E45.11.6.0", {"center": v(250, 0) * mm, "radius": 5 * mm, "construction": true});
            skCircle(sketch, "E45.11.7.0", {"center": v(250, 50) * mm, "radius": 5 * mm, "construction": true});
            skCircle(sketch, "E45.11.8.0", {"center": v(250, 100) * mm, "radius": 5 * mm, "construction": true});
            skCircle(sketch, "E45.11.9.0", {"center": v(250, 150) * mm, "radius": 5 * mm, "construction": true});
            skCircle(sketch, "E45.11.10.0", {"center": v(250, 200) * mm, "radius": 5 * mm, "construction": true});
            skCircle(sketch, "E45.11.11.0", {"center": v(250, 250) * mm, "radius": 5 * mm, "construction": true});
            skCircle(sketch, "E45.11.12.0", {"center": v(250, 300) * mm, "radius": 5 * mm, "construction": true});
            skArc(sketch, "E45.12.0.0", {"start": v(302.5, -295.67) * mm, "mid": v(296.46, -296.46) * mm, "end": v(295.67, -302.5) * mm});
            skCircle(sketch, "E45.12.1.0", {"center": v(300, -250) * mm, "radius": 5 * mm, "construction": true});
            skCircle(sketch, "E45.12.2.0", {"center": v(300, -200) * mm, "radius": 5 * mm, "construction": true});
            skCircle(sketch, "E45.12.3.0", {"center": v(300, -150) * mm, "radius": 5 * mm, "construction": true});
            skCircle(sketch, "E45.12.4.0", {"center": v(300, -100) * mm, "radius": 5 * mm, "construction": true});
            skCircle(sketch, "E45.12.5.0", {"center": v(300, -50) * mm, "radius": 5 * mm, "construction": true});
            skArc(sketch, "E45.12.6.0", {"start": v(302.5, 4.33) * mm, "mid": v(295, 0) * mm, "end": v(302.5, -4.33) * mm});
            skCircle(sketch, "E45.12.7.0", {"center": v(300, 50) * mm, "radius": 5 * mm, "construction": true});
            skCircle(sketch, "E45.12.8.0", {"center": v(300, 100) * mm, "radius": 5 * mm, "construction": true});
            skCircle(sketch, "E45.12.9.0", {"center": v(300, 150) * mm, "radius": 5 * mm, "construction": true});
            skCircle(sketch, "E45.12.10.0", {"center": v(300, 200) * mm, "radius": 5 * mm, "construction": true});
            skCircle(sketch, "E45.12.11.0", {"center": v(300, 250) * mm, "radius": 5 * mm, "construction": true});
            skArc(sketch, "E45.12.12.0", {"start": v(295.67, 302.5) * mm, "mid": v(296.46, 296.46) * mm, "end": v(302.5, 295.67) * mm});
            skLineSegment(sketch, "E45.direction1", {"start": v(-300, -300) * mm, "end": v(-250, -300) * mm, "construction": true});
            skLineSegment(sketch, "E45.direction2", {"start": v(-300, -300) * mm, "end": v(-300, -250) * mm, "construction": true});
            skLineSegment(sketch, "E46.trimOffspring", {"start": v(-4.33, -302.5) * mm, "end": v(-295.67, -302.5) * mm});
            skLineSegment(sketch, "E47.trimOffspring", {"start": v(-302.5, -4.33) * mm, "end": v(-302.5, -295.67) * mm});
            skPoint(sketch, "E48.orphan", {"position": v(-302.5, -302.5) * mm});
            skPoint(sketch, "E49.orphan", {"position": v(-302.5, 302.5) * mm});
            skLineSegment(sketch, "E50.trimOffspring", {"start": v(-4.33, 302.5) * mm, "end": v(-295.67, 302.5) * mm});
            skPoint(sketch, "E51.orphan", {"position": v(302.5, 302.5) * mm});
            skLineSegment(sketch, "E52.trimOffspring", {"start": v(302.5, -4.33) * mm, "end": v(302.5, -295.67) * mm});
            skPoint(sketch, "E53.orphan", {"position": v(302.5, -302.5) * mm});
            skSolve(sketch);
        }
        {
            var Q0;
            Q0 = qSketchRegion(id + "F4", true);
            extrude(context, id + "F5", {"entities" : qUnion([Q0]), "operationType" : NewBodyOperationType.ADD, "depth" : 2 * mm});
        }
    });
